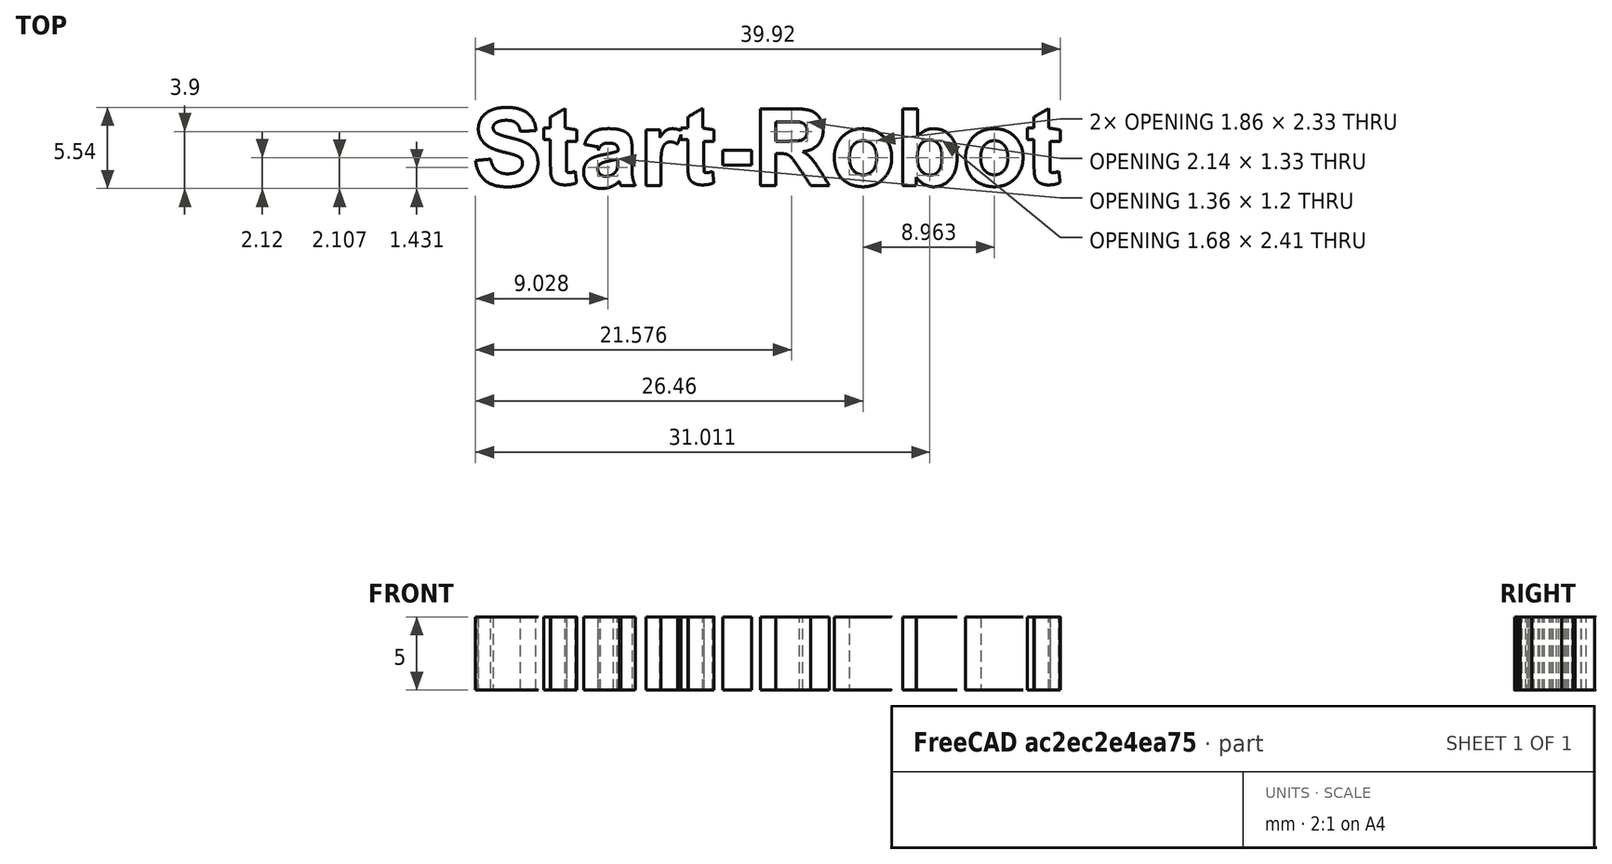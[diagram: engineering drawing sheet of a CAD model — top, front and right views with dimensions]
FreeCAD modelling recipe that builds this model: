
FCSTD DOCUMENT  (FreeCAD 0.14R3700 (Git))
Label: texto
License: CC-BY 3.0
LicenseURL: http://creativecommons.org/licenses/by/3.0/
objects: Part::Feature×16, Part::Extrusion×16, Part::Cut×5, Part::MultiFuse×1
note: 38 computed .brp shape members not serialized (recipe doc carries the construction recipe); baked Part::Feature solids carry a one-line shape summary decoded from their .brp

FEATURE [Part::Feature] path3025
  shape: bbox 4.267 x 5.43 x 2e-07 mm, 0 faces, 0 solids (baked)
FEATURE [Part::Feature] path3027
  shape: bbox 2.248 x 5.23 x 2e-07 mm, 0 faces, 0 solids (baked)
FEATURE [Part::Feature] path3029
  shape: bbox 3.533 x 4.091 x 2e-07 mm, 0 faces, 0 solids (baked)
FEATURE [Part::Feature] path3029001
  shape: bbox 1.357 x 1.203 x 2e-07 mm, 0 faces, 0 solids (baked)
FEATURE [Part::Feature] path3031
  shape: bbox 2.463 x 3.887 x 2e-07 mm, 0 faces, 0 solids (baked)
FEATURE [Part::Feature] path3033
  shape: bbox 2.248 x 5.23 x 2e-07 mm, 0 faces, 0 solids (baked)
FEATURE [Part::Feature] path3035
  shape: bbox 1.976 x 1.006 x 2e-07 mm, 0 faces, 0 solids (baked)
FEATURE [Part::Feature] path3037
  shape: bbox 4.718 x 5.247 x 2e-07 mm, 0 faces, 0 solids (baked)
FEATURE [Part::Feature] path3037001
  shape: bbox 2.14 x 1.332 x 2e-07 mm, 0 faces, 0 solids (baked)
FEATURE [Part::Feature] path3039
  shape: bbox 3.923 x 3.973 x 2e-07 mm, 0 faces, 0 solids (baked)
FEATURE [Part::Feature] path3039001
  shape: bbox 1.858 x 2.334 x 2e-07 mm, 0 faces, 0 solids (baked)
FEATURE [Part::Feature] path3041
  shape: bbox 3.712 x 5.333 x 2e-07 mm, 0 faces, 0 solids (baked)
FEATURE [Part::Feature] path3041001
  shape: bbox 1.682 x 2.409 x 2e-07 mm, 0 faces, 0 solids (baked)
FEATURE [Part::Feature] path3043
  shape: bbox 3.923 x 3.973 x 2e-07 mm, 0 faces, 0 solids (baked)
FEATURE [Part::Feature] path3043001
  shape: bbox 1.858 x 2.334 x 2e-07 mm, 0 faces, 0 solids (baked)
FEATURE [Part::Feature] path3045
  shape: bbox 2.248 x 5.23 x 2e-07 mm, 0 faces, 0 solids (baked)
FEATURE [Part::Extrusion] Extrude
  Base = -> path3025
  Dir = (0,0,5)
  Solid = true
FEATURE [Part::Extrusion] Extrude001
  Base = -> path3027
  Dir = (0,0,5)
  Solid = true
FEATURE [Part::Extrusion] Extrude002
  Base = -> path3029
  Dir = (0,0,5)
  Solid = true
FEATURE [Part::Extrusion] Extrude003
  Base = -> path3029001
  Dir = (0,0,5)
  Solid = true
FEATURE [Part::Extrusion] Extrude004
  Base = -> path3031
  Dir = (0,0,5)
  Solid = true
FEATURE [Part::Extrusion] Extrude005
  Base = -> path3033
  Dir = (0,0,5)
  Solid = true
FEATURE [Part::Extrusion] Extrude006
  Base = -> path3035
  Dir = (0,0,5)
  Solid = true
FEATURE [Part::Extrusion] Extrude007
  Base = -> path3037
  Dir = (0,0,5)
  Solid = true
FEATURE [Part::Extrusion] Extrude008
  Base = -> path3037001
  Dir = (0,0,5)
  Solid = true
FEATURE [Part::Extrusion] Extrude009
  Base = -> path3039
  Dir = (0,0,5)
  Solid = true
FEATURE [Part::Extrusion] Extrude010
  Base = -> path3039001
  Dir = (0,0,5)
  Solid = true
FEATURE [Part::Extrusion] Extrude011
  Base = -> path3041
  Dir = (0,0,5)
  Solid = true
FEATURE [Part::Extrusion] Extrude012
  Base = -> path3041001
  Dir = (0,0,5)
  Solid = true
FEATURE [Part::Extrusion] Extrude013
  Base = -> path3043
  Dir = (0,0,5)
  Solid = true
FEATURE [Part::Extrusion] Extrude014
  Base = -> path3043001
  Dir = (0,0,5)
  Solid = true
FEATURE [Part::Extrusion] Extrude015
  Base = -> path3045
  Dir = (0,0,5)
  Solid = true
FEATURE [Part::Cut] Cut
  Base = -> Extrude002
  Tool = -> Extrude003
FEATURE [Part::Cut] Cut001
  Base = -> Extrude007
  Tool = -> Extrude008
FEATURE [Part::Cut] Cut002
  Base = -> Extrude009
  Tool = -> Extrude010
FEATURE [Part::Cut] Cut003
  Base = -> Extrude011
  Tool = -> Extrude012
FEATURE [Part::Cut] Cut004
  Base = -> Extrude013
  Tool = -> Extrude014
FEATURE [Part::MultiFuse] Fusion  label="Nombre"
  Shapes = -> [Extrude,Extrude006,Cut001,Cut,Extrude004,Extrude005,Extrude015,Cut003,Cut004,Extrude001,Cut002]
